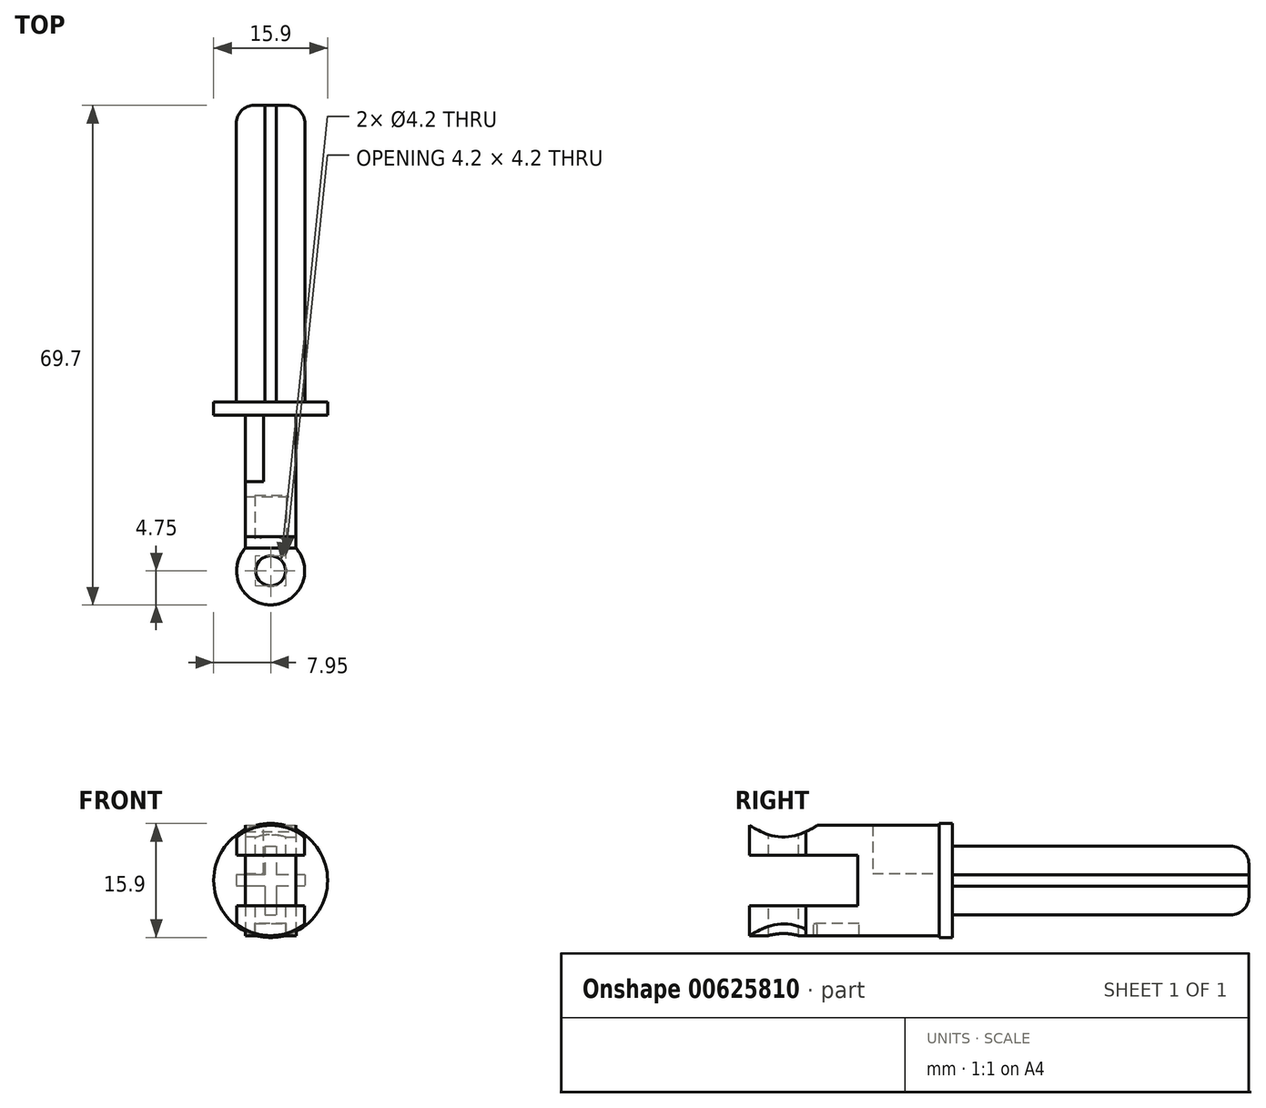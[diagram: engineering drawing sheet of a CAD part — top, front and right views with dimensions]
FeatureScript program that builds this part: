
annotation { "Feature Type Name" : "Feature", "Feature Type Description" : "" }
export const myFeature = defineFeature(function(context is Context, id is Id, definition is map)
    precondition{}
    {
        {
            var Q0;
            Q0=qCreatedBy(makeId("Front.planeOp"),FACE);
            var sketch = newSketch(context, id + "F0", { "sketchPlane" : qUnion([Q0])});
            skCircle(sketch, "E0", {"center": v(0, 0) * mm, "radius": 7.95 * mm});
            skSolve(sketch);
        }
        {
            var Q0;
            Q0 = qSketchRegion(id + "F0", true);
            extrude(context, id + "F1", {"entities" : qUnion([Q0]), "oppositeDirection" : true, "depth" : 1.8 * mm, "offsetDistance" : 25 * mm});
        }
        {
            var Q0;
            Q0=makeQuery(id+"F1.opExtrude","CAP_FACE",FACE,{"disambiguationData":[OSD([sQuery(id+"F0.wireOp",EDGE,"E0")])],"isStart":false});
            var sketch = newSketch(context, id + "F2", { "sketchPlane" : qUnion([Q0])});
            skLineSegment(sketch, "E1.bottom", {"start": v(0.8, 4.8) * mm, "end": v(-0.8, 4.8) * mm});
            skLineSegment(sketch, "E1.top", {"start": v(0.8, -4.8) * mm, "end": v(-0.8, -4.8) * mm});
            skLineSegment(sketch, "E1.left", {"start": v(0.8, 4.8) * mm, "end": v(0.8, 0.8) * mm});
            skLineSegment(sketch, "E1.right", {"start": v(-0.8, 4.8) * mm, "end": v(-0.8, 0.8) * mm});
            skPoint(sketch, "E1.middle", {"position": v(0, 0) * mm});
            skLineSegment(sketch, "E2.bottom", {"start": v(-4.8, 0.8) * mm, "end": v(-0.8, 0.8) * mm});
            skLineSegment(sketch, "E2.top", {"start": v(-4.8, -0.8) * mm, "end": v(-0.8, -0.8) * mm});
            skLineSegment(sketch, "E2.left", {"start": v(-4.8, 0.8) * mm, "end": v(-4.8, -0.8) * mm});
            skLineSegment(sketch, "E2.right", {"start": v(4.8, 0.8) * mm, "end": v(4.8, -0.8) * mm});
            skLineSegment(sketch, "E3.trimOffspring", {"start": v(-0.8, -0.8) * mm, "end": v(-0.8, -4.8) * mm});
            skLineSegment(sketch, "E4.trimOffspring", {"start": v(0.8, 0.8) * mm, "end": v(4.8, 0.8) * mm});
            skLineSegment(sketch, "E5.trimOffspring", {"start": v(0.8, -0.8) * mm, "end": v(4.8, -0.8) * mm});
            skLineSegment(sketch, "E6.trimOffspring", {"start": v(0.8, -0.8) * mm, "end": v(0.8, -4.8) * mm});
            skSolve(sketch);
        }
        {
            var Q0;
            Q0 = qSketchRegion(id + "F2", true);
            extrude(context, id + "F3", {"entities" : qUnion([Q0]), "operationType" : NewBodyOperationType.ADD, "depth" : 41.4 * mm, "offsetDistance" : 25 * mm});
        }
        {
            var Q0;
            Q0=qCreatedBy(makeId("Front.planeOp"),FACE);
            cPlane(context, id + "F4", {"entities" : qUnion([Q0]), "cplaneType" : CPlaneType.OFFSET, "offset" : 9.3 * mm, "width" : 150 * mm, "height" : 150 * mm});
        }
        {
            var Q0;
            Q0=qCreatedBy(makeId("Front.planeOp"),FACE);
            var sketch = newSketch(context, id + "F5", { "sketchPlane" : qUnion([Q0])});
            skLineSegment(sketch, "E7.bottom", {"start": v(-3.55, 7.7) * mm, "end": v(3.55, 7.7) * mm});
            skLineSegment(sketch, "E7.top", {"start": v(-3.55, -7.7) * mm, "end": v(3.55, -7.7) * mm});
            skLineSegment(sketch, "E7.left", {"start": v(-3.55, 7.7) * mm, "end": v(-3.55, -7.7) * mm});
            skLineSegment(sketch, "E7.right", {"start": v(3.55, 7.7) * mm, "end": v(3.55, -7.7) * mm});
            skLineSegment(sketch, "E8", {"start": v(0, 20.04) * mm, "end": v(0, -21.13) * mm, "construction": true});
            skLineSegment(sketch, "E9", {"start": v(-19.78, 0) * mm, "end": v(20.58, 0) * mm, "construction": true});
            skPoint(sketch, "E10", {"position": v(3.55, 0) * mm});
            skPoint(sketch, "E11", {"position": v(0, 7.7) * mm});
            skSolve(sketch);
        }
        {
            var Q0;
            Q0 = qSketchRegion(id + "F5", true);
            extrude(context, id + "F6", {"entities" : qUnion([Q0]), "operationType" : NewBodyOperationType.ADD, "depth" : 9.3 * mm, "offsetDistance" : 25 * mm});
        }
        {
            var Q0;
            Q0=makeQuery(id+"F6.opExtrude","SWEPT_FACE",FACE,{"disambiguationData":[OSD([sQuery(id+"F5.wireOp",EDGE,"E7.bottom")])]});
            var sketch = newSketch(context, id + "F7", { "sketchPlane" : qUnion([Q0])});
            skLineSegment(sketch, "E12.bottom", {"start": v(-3.55, 0) * mm, "end": v(-1, 0) * mm});
            skLineSegment(sketch, "E12.top", {"start": v(-3.55, -9.3) * mm, "end": v(-1, -9.3) * mm});
            skLineSegment(sketch, "E12.left", {"start": v(-3.55, 0) * mm, "end": v(-3.55, -9.3) * mm});
            skLineSegment(sketch, "E12.right", {"start": v(-1, 0) * mm, "end": v(-1, -9.3) * mm});
            skSolve(sketch);
        }
        {
            var Q0;
            Q0 = qSketchRegion(id + "F7", true);
            extrude(context, id + "F8", {"entities" : qUnion([Q0]), "operationType" : NewBodyOperationType.REMOVE, "oppositeDirection" : true, "depth" : 6.75 * mm, "offsetDistance" : 25 * mm});
        }
        {
            var Q0;
            Q0=qCreatedBy(id+"F4.planeOp",FACE);
            var sketch = newSketch(context, id + "F9", { "sketchPlane" : qUnion([Q0])});
            skLineSegment(sketch, "E13.bottom", {"start": v(-3.55, 7.7) * mm, "end": v(3.55, 7.7) * mm});
            skLineSegment(sketch, "E13.top", {"start": v(-3.55, -7.7) * mm, "end": v(3.55, -7.7) * mm});
            skLineSegment(sketch, "E13.left", {"start": v(-3.55, 7.7) * mm, "end": v(-3.55, -7.7) * mm});
            skLineSegment(sketch, "E13.right", {"start": v(3.55, 7.7) * mm, "end": v(3.55, -7.7) * mm});
            skLineSegment(sketch, "E14.0", {"start": v(-1, 7.7) * mm, "end": v(1, 7.7) * mm});
            skLineSegment(sketch, "E15.0", {"start": v(3.55, 0.95) * mm, "end": v(3.55, -0.95) * mm});
            skSolve(sketch);
        }
        {
            var Q0;
            Q0 = qSketchRegion(id + "F9", true);
            extrude(context, id + "F10", {"entities" : qUnion([Q0]), "operationType" : NewBodyOperationType.ADD, "depth" : 12.7 * mm, "offsetDistance" : 25 * mm});
        }
        {
            var Q0;
            Q0=qCreatedBy(makeId("Top.planeOp"),FACE);
            var sketch = newSketch(context, id + "F11", { "sketchPlane" : qUnion([Q0])});
            skCircle(sketch, "E16", {"center": v(0, -21.75) * mm, "radius": 4.75 * mm});
            skSolve(sketch);
        }
        {
            var Q0;
            Q0 = qSketchRegion(id + "F11", true);
            var Q1;
            Q1=makeQuery(id+"F10.boolean.opBoolean","MERGE",FACE,{"derivedFrom":[makeQuery(id+"F6.opExtrude","SWEPT_FACE",FACE,{"disambiguationData":[OSD([sQuery(id+"F5.wireOp",EDGE,"E7.bottom")])]}),makeQuery(id+"F10.opExtrude","SWEPT_FACE",FACE,{"disambiguationData":[OSD([sQuery(id+"F9.wireOp",EDGE,"E13.bottom"),sQuery(id+"F9.wireOp",EDGE,"E14.0")])]})]});
            var Q2;
            Q2=makeQuery(id+"F10.boolean.opBoolean","MERGE",FACE,{"derivedFrom":[makeQuery(id+"F6.opExtrude","SWEPT_FACE",FACE,{"disambiguationData":[OSD([sQuery(id+"F5.wireOp",EDGE,"E7.top")])]}),makeQuery(id+"F10.opExtrude","SWEPT_FACE",FACE,{"disambiguationData":[OSD([sQuery(id+"F9.wireOp",EDGE,"E13.top")])]})]});
            extrude(context, id + "F12", {"entities" : qUnion([Q0]), "operationType" : NewBodyOperationType.ADD, "endBound" : BoundingType.UP_TO_SURFACE, "depth" : 25 * mm, "endBoundEntityFace" : qUnion([Q1]), "offsetDistance" : 25 * mm, "hasSecondDirection" : true, "secondDirectionBound" : SecondDirectionBoundingType.UP_TO_SURFACE, "secondDirectionOppositeDirection" : true, "secondDirectionDepth" : 25 * mm, "secondDirectionBoundEntityFace" : qUnion([Q2])});
        }
        {
            var Q0;
            Q0=qCreatedBy(id+"F4.planeOp",FACE);
            cPlane(context, id + "F13", {"entities" : qUnion([Q0]), "cplaneType" : CPlaneType.OFFSET, "offset" : 17.5 * mm, "width" : 150 * mm, "height" : 150 * mm});
        }
        {
            var Q0;
            Q0=qCreatedBy(id+"F13.planeOp",FACE);
            var sketch = newSketch(context, id + "F14", { "sketchPlane" : qUnion([Q0])});
            skCircle(sketch, "E17", {"center": v(0, 0) * mm, "radius": 7.7 * mm});
            skLineSegment(sketch, "E18.bottom", {"start": v(-7.7, 7.7) * mm, "end": v(7.7, 7.7) * mm});
            skLineSegment(sketch, "E18.top", {"start": v(-7.7, -7.7) * mm, "end": v(7.7, -7.7) * mm});
            skLineSegment(sketch, "E18.left", {"start": v(-7.7, 7.7) * mm, "end": v(-7.7, -7.7) * mm});
            skLineSegment(sketch, "E18.right", {"start": v(7.7, 7.7) * mm, "end": v(7.7, -7.7) * mm});
            skSolve(sketch);
        }
        {
            var Q0;
            {var subQ0=sQuery(id+"F14.wireOp",EDGE,"E18.bottom");var subQ1=sQuery(id+"F14.wireOp",EDGE,"E17");var subQ2=makeQuery(id+"F14.imprint","INTERSECT",VERTEX,{"derivedFrom":[subQ1,subQ0]});Q0=makeQuery(id+"F14.imprint","IMPRINT",FACE,{"disambiguationData":[TD([[makeQuery(id+"F14.imprint","IMPRINT",EDGE,{"disambiguationData":[TD([[subQ2,1.0]])],"derivedFrom":subQ1}),-1.0]])]});}
            var Q1;
            {var subQ0=sQuery(id+"F14.wireOp",EDGE,"E18.bottom");var subQ1=sQuery(id+"F14.wireOp",EDGE,"E17");var subQ2=makeQuery(id+"F14.imprint","INTERSECT",VERTEX,{"derivedFrom":[subQ1,subQ0]});Q1=makeQuery(id+"F14.imprint","IMPRINT",FACE,{"disambiguationData":[TD([[makeQuery(id+"F14.imprint","IMPRINT",EDGE,{"disambiguationData":[TD([[subQ2,-1.0]])],"derivedFrom":subQ1}),-1.0]])]});}
            var Q2;
            {var subQ0=sQuery(id+"F14.wireOp",EDGE,"E18.left");var subQ1=sQuery(id+"F14.wireOp",EDGE,"E17");var subQ2=makeQuery(id+"F14.imprint","INTERSECT",VERTEX,{"derivedFrom":[subQ1,subQ0]});Q2=makeQuery(id+"F14.imprint","IMPRINT",FACE,{"disambiguationData":[TD([[makeQuery(id+"F14.imprint","IMPRINT",EDGE,{"disambiguationData":[TD([[subQ2,-1.0]])],"derivedFrom":subQ1}),-1.0]])]});}
            var Q3;
            {var subQ0=sQuery(id+"F14.wireOp",EDGE,"E18.right");var subQ1=sQuery(id+"F14.wireOp",EDGE,"E17");var subQ2=makeQuery(id+"F14.imprint","INTERSECT",VERTEX,{"derivedFrom":[subQ1,subQ0]});Q3=makeQuery(id+"F14.imprint","IMPRINT",FACE,{"disambiguationData":[TD([[makeQuery(id+"F14.imprint","IMPRINT",EDGE,{"disambiguationData":[TD([[subQ2,1.0]])],"derivedFrom":subQ1}),-1.0]])]});}
            extrude(context, id + "F15", {"entities" : qUnion([Q0, Q1, Q2, Q3]), "operationType" : NewBodyOperationType.REMOVE, "oppositeDirection" : true, "depth" : 8.2 * mm, "offsetDistance" : 25 * mm});
        }
        {
            var Q0;
            Q0=qCreatedBy(id+"F13.planeOp",FACE);
            var sketch = newSketch(context, id + "F16", { "sketchPlane" : qUnion([Q0])});
            skLineSegment(sketch, "E19.bottom", {"start": v(-8.52, 3.5) * mm, "end": v(9.15, 3.5) * mm});
            skLineSegment(sketch, "E19.top", {"start": v(-8.52, -3.5) * mm, "end": v(9.15, -3.5) * mm});
            skLineSegment(sketch, "E19.left", {"start": v(-8.52, 3.5) * mm, "end": v(-8.52, -3.5) * mm});
            skLineSegment(sketch, "E19.right", {"start": v(9.15, 3.5) * mm, "end": v(9.15, -3.5) * mm});
            skLineSegment(sketch, "E20", {"start": v(4.75, 6.06) * mm, "end": v(4.75, -6.06) * mm});
            skLineSegment(sketch, "E21", {"start": v(-4.75, -6.06) * mm, "end": v(-4.75, 6.06) * mm});
            skPoint(sketch, "E22", {"position": v(4.75, 0) * mm});
            skPoint(sketch, "E23", {"position": v(-8.52, 0) * mm});
            skSolve(sketch);
        }
        {
            var Q0;
            Q0 = qSketchRegion(id + "F16", true);
            extrude(context, id + "F17", {"entities" : qUnion([Q0]), "operationType" : NewBodyOperationType.REMOVE, "oppositeDirection" : true, "depth" : 15.4 * mm, "offsetDistance" : 25 * mm});
        }
        {
            var Q0;
            Q0=qCreatedBy(makeId("Top.planeOp"),FACE);
            var sketch = newSketch(context, id + "F18", { "sketchPlane" : qUnion([Q0])});
            skArc(sketch, "E24.0", {"start": v(3.56, -18.6) * mm, "mid": v(0, -26.5) * mm, "end": v(-3.56, -18.6) * mm});
            skCircle(sketch, "E25", {"center": v(0, -21.75) * mm, "radius": 2.1 * mm});
            skSolve(sketch);
        }
        {
            var Q0;
            Q0 = qSketchRegion(id + "F18", true);
            extrude(context, id + "F19", {"entities" : qUnion([Q0]), "operationType" : NewBodyOperationType.REMOVE, "endBound" : BoundingType.THROUGH_ALL, "oppositeDirection" : true, "depth" : 25 * mm, "offsetDistance" : 25 * mm, "hasSecondDirection" : true, "secondDirectionOppositeDirection" : false, "secondDirectionDepth" : 25 * mm});
        }
        {
            var Q0;
            Q0=makeQuery(id+"F3.opExtrude","CAP_EDGE",EDGE,{"disambiguationData":[OSD([sQuery(id+"F2.wireOp",EDGE,"E1.bottom")])],"isStart":false});
            var Q1;
            Q1=makeQuery(id+"F3.opExtrude","CAP_EDGE",EDGE,{"disambiguationData":[OSD([sQuery(id+"F2.wireOp",EDGE,"E2.left")])],"isStart":false});
            var Q2;
            Q2=makeQuery(id+"F3.opExtrude","CAP_EDGE",EDGE,{"disambiguationData":[OSD([sQuery(id+"F2.wireOp",EDGE,"E1.top")])],"isStart":false});
            var Q3;
            Q3=makeQuery(id+"F3.opExtrude","CAP_EDGE",EDGE,{"disambiguationData":[OSD([sQuery(id+"F2.wireOp",EDGE,"E2.right")])],"isStart":false});
            fillet(context, id + "F20", {"entities" : qUnion([Q0, Q1, Q2, Q3]), "radius" : 2.5 * mm, "tangentPropagation" : true, "allowEdgeOverflow" : false});
        }
        {
            var Q0;
            Q0=qCreatedBy(makeId("Top.planeOp"),FACE);
            cPlane(context, id + "F21", {"entities" : qUnion([Q0]), "cplaneType" : CPlaneType.OFFSET, "offset" : 6 * mm, "oppositeDirection" : true, "width" : 150 * mm, "height" : 150 * mm});
        }
        {
            var Q0;
            Q0=qCreatedBy(id+"F21.planeOp",FACE);
            var sketch = newSketch(context, id + "F22", { "sketchPlane" : qUnion([Q0])});
            skCircle(sketch, "E26.0", {"center": v(0, -21.75) * mm, "radius": 2.1 * mm});
            skArc(sketch, "E27", {"start": v(2.2, -17.54) * mm, "mid": v(0, -17) * mm, "end": v(-2.2, -17.54) * mm});
            skLineSegment(sketch, "E28.bottom", {"start": v(-2.2, -11.2) * mm, "end": v(2.2, -11.2) * mm});
            skLineSegment(sketch, "E28.left", {"start": v(-2.2, -11.2) * mm, "end": v(-2.2, -17.54) * mm});
            skLineSegment(sketch, "E28.right", {"start": v(2.2, -11.2) * mm, "end": v(2.2, -17.54) * mm});
            skSolve(sketch);
        }
        {
            var Q0;
            Q0 = qSketchRegion(id + "F22", true);
            extrude(context, id + "F23", {"entities" : qUnion([Q0]), "operationType" : NewBodyOperationType.REMOVE, "oppositeDirection" : true, "depth" : 25 * mm, "offsetDistance" : 25 * mm});
        }
        {
            var Q0;
            Q0=qCreatedBy(makeId("Right.planeOp"),FACE);
            var sketch = newSketch(context, id + "F24", { "sketchPlane" : qUnion([Q0])});
            skLineSegment(sketch, "E29.0", {"start": v(-17.54, 7.7) * mm, "end": v(-17, 7.7) * mm});
            skFitSpline(sketch, "E30.0", {"points": [v(-18.6, 6.83) * mm, v(-18.77, 6.75) * mm, v(-19.12, 6.6) * mm, v(-19.7, 6.39) * mm, v(-20.34, 6.21) * mm, v(-20.9, 6.11) * mm, v(-21.35, 6.07) * mm, v(-21.83, 6.05) * mm, v(-22.4, 6.08) * mm, v(-23.1, 6.2) * mm, v(-23.73, 6.37) * mm, v(-24.32, 6.58) * mm, v(-24.85, 6.8) * mm, v(-25.33, 7.04) * mm, v(-25.87, 7.32) * mm, v(-26.36, 7.61) * mm, v(-26.5, 7.7) * mm, v(-26.5, 7.7) * mm]});
            skArc(sketch, "E31", {"start": v(-18.6, 6.83) * mm, "mid": v(-20.84, 22.8) * mm, "end": v(-26.5, 7.7) * mm});
            skSolve(sketch);
        }
        {
            var Q0;
            Q0 = qSketchRegion(id + "F24", true);
            extrude(context, id + "F25", {"entities" : qUnion([Q0]), "operationType" : NewBodyOperationType.REMOVE, "endBound" : BoundingType.SYMMETRIC, "oppositeDirection" : true, "depth" : 25 * mm, "offsetDistance" : 25 * mm});
        }
    });
